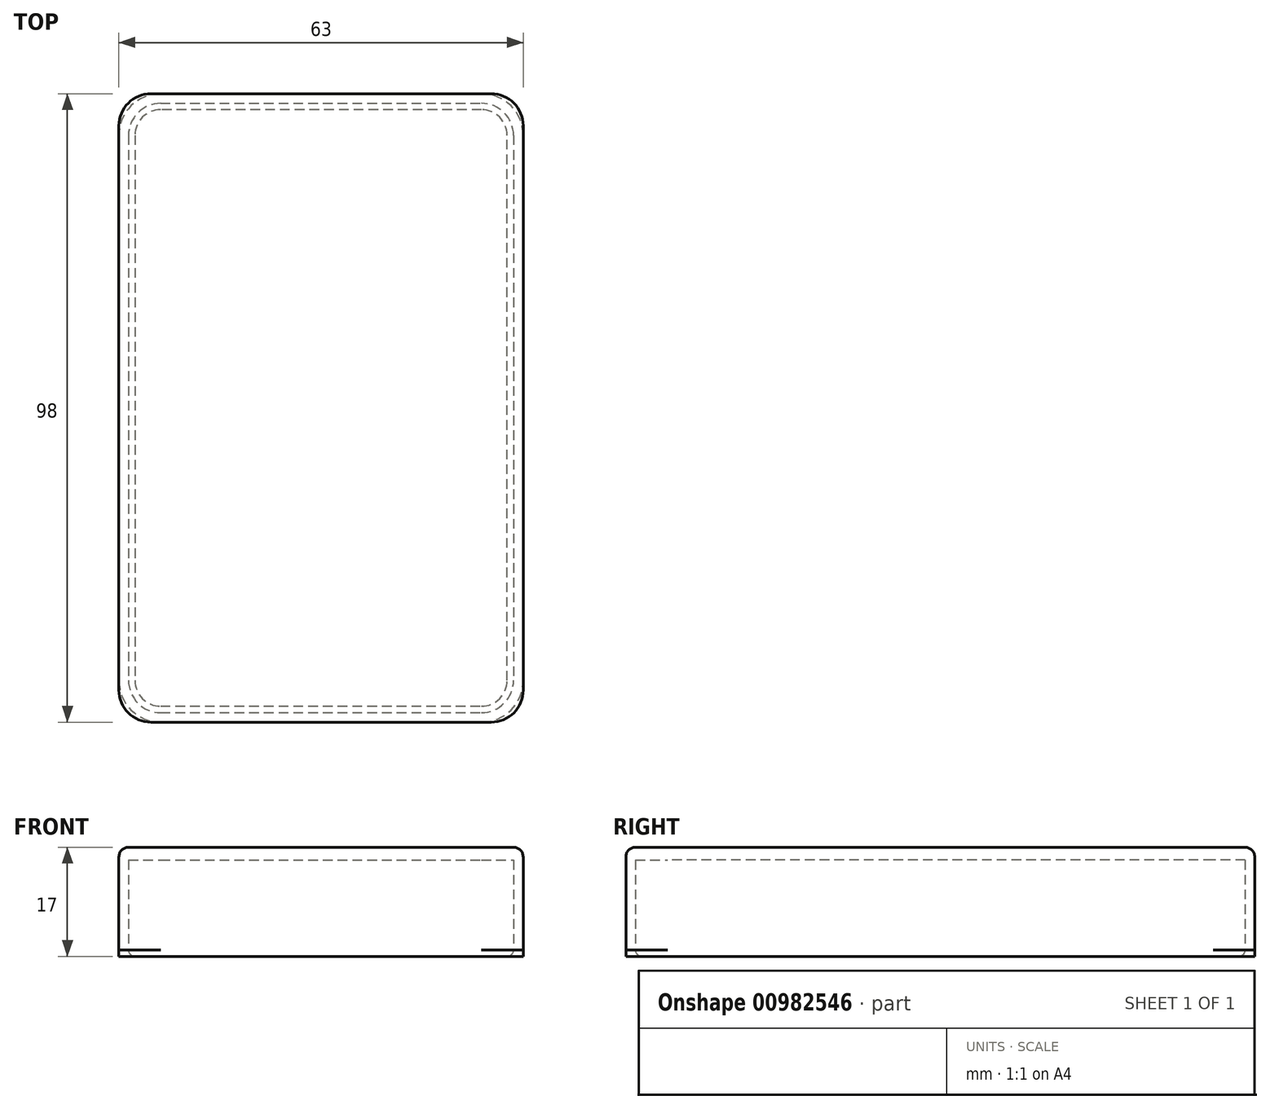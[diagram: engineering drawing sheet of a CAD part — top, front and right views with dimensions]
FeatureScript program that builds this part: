
annotation { "Feature Type Name" : "Feature", "Feature Type Description" : "" }
export const myFeature = defineFeature(function(context is Context, id is Id, definition is map)
    precondition{}
    {
        {
            var Q0;
            Q0=qCreatedBy(makeId("Top.planeOp"),FACE);
            var sketch = newSketch(context, id + "F0", { "sketchPlane" : qUnion([Q0])});
            skLineSegment(sketch, "E0.bottom", {"start": v(-30, 47.5) * mm, "end": v(30, 47.5) * mm});
            skLineSegment(sketch, "E0.top", {"start": v(-30, -47.5) * mm, "end": v(30, -47.5) * mm});
            skLineSegment(sketch, "E0.left", {"start": v(-30, 47.5) * mm, "end": v(-30, -47.5) * mm});
            skLineSegment(sketch, "E0.right", {"start": v(30, 47.5) * mm, "end": v(30, -47.5) * mm});
            skLineSegment(sketch, "E1", {"start": v(-30, 47.5) * mm, "end": v(30, -47.5) * mm, "construction": true});
            skLineSegment(sketch, "E2", {"start": v(30, 47.5) * mm, "end": v(-30, -47.5) * mm, "construction": true});
            skPoint(sketch, "E3", {"position": v(0, 0) * mm});
            skSolve(sketch);
        }
        {
            var Q0;
            Q0=qCreatedBy(makeId("Top.planeOp"),FACE);
            var sketch = newSketch(context, id + "F1", { "sketchPlane" : qUnion([Q0])});
            skLineSegment(sketch, "E4.0", {"start": v(-31.5, 49) * mm, "end": v(-31.5, -49) * mm});
            skLineSegment(sketch, "E4.1", {"start": v(31.5, 49) * mm, "end": v(-31.5, 49) * mm});
            skLineSegment(sketch, "E4.2", {"start": v(31.5, -49) * mm, "end": v(31.5, 49) * mm});
            skLineSegment(sketch, "E4.3", {"start": v(-31.5, -49) * mm, "end": v(31.5, -49) * mm});
            skSolve(sketch);
        }
        {
            var Q0;
            Q0=makeQuery(id+"F1.imprint","IMPRINT",FACE,{"disambiguationData":[TD([[makeQuery(id+"F1.imprint","IMPRINT",EDGE,{"derivedFrom":sQuery(id+"F1.wireOp",EDGE,"E4.0")}),1.0]])]});
            var Q1;
            Q1=sQuery(id+"F1.wireOp",EDGE,"E4.3");
            var Q2;
            Q2=sQuery(id+"F1.wireOp",EDGE,"E4.2");
            var Q3;
            Q3=sQuery(id+"F1.wireOp",EDGE,"E4.0");
            var Q4;
            Q4=sQuery(id+"F0.wireOp",EDGE,"E0.right");
            var Q5;
            Q5=sQuery(id+"F0.wireOp",EDGE,"E0.top");
            var Q6;
            Q6=sQuery(id+"F0.wireOp",EDGE,"E0.bottom");
            var Q7;
            Q7=sQuery(id+"F1.wireOp",EDGE,"E4.1");
            var Q8;
            Q8=sQuery(id+"F0.wireOp",EDGE,"E0.left");
            extrude(context, id + "F2", {"entities" : qUnion([Q0]), "surfaceEntities" : qUnion([Q1, Q2, Q3, Q4, Q5, Q6, Q7, Q8]), "depth" : 16 * mm, "offsetDistance" : 25 * mm});
        }
        {
            var Q0;
            Q0 = qSketchRegion(id + "F0", true);
            var Q1;
            Q1=makeQuery(id+"F2.opExtrude","CAP_FACE",FACE,{"disambiguationData":[OSD([sQuery(id+"F1.wireOp",EDGE,"E4.0"),sQuery(id+"F1.wireOp",EDGE,"E4.1"),sQuery(id+"F1.wireOp",EDGE,"E4.2"),sQuery(id+"F1.wireOp",EDGE,"E4.3")])],"isStart":false});
            extrude(context, id + "F3", {"entities" : qUnion([Q0]), "operationType" : NewBodyOperationType.REMOVE, "endBound" : BoundingType.UP_TO_SURFACE, "depth" : 25 * mm, "endBoundEntityFace" : qUnion([Q1]), "hasOffset" : true, "offsetDistance" : 2 * mm});
        }
        {
            var Q0;
            Q0=makeQuery(id+"F3.boolean.opBoolean","COPY",EDGE,{"derivedFrom":makeQuery(id+"F3.opExtrude","SWEPT_EDGE",EDGE,{"disambiguationData":[OSD([sQuery(id+"F0.wireOp",EDGE,"E0.bottom"),sQuery(id+"F0.wireOp",EDGE,"E0.left")])]})});
            var Q1;
            Q1=makeQuery(id+"F3.boolean.opBoolean","COPY",EDGE,{"derivedFrom":makeQuery(id+"F3.opExtrude","SWEPT_EDGE",EDGE,{"disambiguationData":[OSD([sQuery(id+"F0.wireOp",EDGE,"E0.bottom"),sQuery(id+"F0.wireOp",EDGE,"E0.right")])]})});
            var Q2;
            Q2=makeQuery(id+"F2.opExtrude","SWEPT_EDGE",EDGE,{"disambiguationData":[OSD([sQuery(id+"F1.wireOp",EDGE,"E4.1"),sQuery(id+"F1.wireOp",EDGE,"E4.2")])]});
            var Q3;
            Q3=makeQuery(id+"F2.opExtrude","SWEPT_EDGE",EDGE,{"disambiguationData":[OSD([sQuery(id+"F1.wireOp",EDGE,"E4.0"),sQuery(id+"F1.wireOp",EDGE,"E4.1")])]});
            var Q4;
            Q4=makeQuery(id+"F2.opExtrude","SWEPT_EDGE",EDGE,{"disambiguationData":[OSD([sQuery(id+"F1.wireOp",EDGE,"E4.0"),sQuery(id+"F1.wireOp",EDGE,"E4.3")])]});
            var Q5;
            Q5=makeQuery(id+"F3.boolean.opBoolean","COPY",EDGE,{"derivedFrom":makeQuery(id+"F3.opExtrude","SWEPT_EDGE",EDGE,{"disambiguationData":[OSD([sQuery(id+"F0.wireOp",EDGE,"E0.top"),sQuery(id+"F0.wireOp",EDGE,"E0.left")])]})});
            var Q6;
            Q6=makeQuery(id+"F3.boolean.opBoolean","COPY",EDGE,{"derivedFrom":makeQuery(id+"F3.opExtrude","SWEPT_EDGE",EDGE,{"disambiguationData":[OSD([sQuery(id+"F0.wireOp",EDGE,"E0.top"),sQuery(id+"F0.wireOp",EDGE,"E0.right")])]})});
            var Q7;
            Q7=makeQuery(id+"F2.opExtrude","SWEPT_EDGE",EDGE,{"disambiguationData":[OSD([sQuery(id+"F1.wireOp",EDGE,"E4.2"),sQuery(id+"F1.wireOp",EDGE,"E4.3")])]});
            fillet(context, id + "F4", {"entities" : qUnion([Q0, Q1, Q2, Q3, Q4, Q5, Q6, Q7]), "tangentPropagation" : true, "radius" : 5 * mm, "defaultsChanged" : false, "vertexSettings" : [], "allowEdgeOverflow" : false});
        }
        {
            var Q0;
            Q0=makeQuery(id+"F2.opExtrude","CAP_FACE",FACE,{"disambiguationData":[OSD([sQuery(id+"F1.wireOp",EDGE,"E4.0"),sQuery(id+"F1.wireOp",EDGE,"E4.1"),sQuery(id+"F1.wireOp",EDGE,"E4.2"),sQuery(id+"F1.wireOp",EDGE,"E4.3")])],"isStart":false});
            fillet(context, id + "F5", {"entities" : qUnion([Q0]), "tangentPropagation" : true, "radius" : 1.5 * mm, "defaultsChanged" : false, "vertexSettings" : [], "allowEdgeOverflow" : false});
        }
        {
            var Q0;
            Q0=qCreatedBy(makeId("Top.planeOp"),FACE);
            var sketch = newSketch(context, id + "F6", { "sketchPlane" : qUnion([Q0])});
            skLineSegment(sketch, "E5.0.0", {"start": v(25, -47.5) * mm, "end": v(-25, -47.5) * mm});
            skArc(sketch, "E5.0.1", {"start": v(-25, -47.5) * mm, "mid": v(-28.54, -46.04) * mm, "end": v(-30, -42.5) * mm});
            skLineSegment(sketch, "E5.0.2", {"start": v(-30, -42.5) * mm, "end": v(-30, 42.5) * mm});
            skArc(sketch, "E5.0.3", {"start": v(-30, 42.5) * mm, "mid": v(-28.54, 46.04) * mm, "end": v(-25, 47.5) * mm});
            skLineSegment(sketch, "E5.0.4", {"start": v(-25, 47.5) * mm, "end": v(25, 47.5) * mm});
            skArc(sketch, "E5.0.5", {"start": v(25, 47.5) * mm, "mid": v(28.54, 46.04) * mm, "end": v(30, 42.5) * mm});
            skLineSegment(sketch, "E5.0.6", {"start": v(30, 42.5) * mm, "end": v(30, -42.5) * mm});
            skArc(sketch, "E5.0.7", {"start": v(30, -42.5) * mm, "mid": v(28.54, -46.04) * mm, "end": v(25, -47.5) * mm});
            skSolve(sketch);
        }
        {
            var Q0;
            Q0=qCreatedBy(makeId("Front.planeOp"),FACE);
            var sketch = newSketch(context, id + "F7", { "sketchPlane" : qUnion([Q0])});
            skPoint(sketch, "E6.0", {"position": v(-30, 0) * mm});
            skPoint(sketch, "E7.0", {"position": v(-31.5, 0) * mm});
            skLineSegment(sketch, "E8", {"start": v(-30, 0) * mm, "end": v(-31.5, 0) * mm});
            skLineSegment(sketch, "E9", {"start": v(-31.5, 0) * mm, "end": v(-31.5, -1) * mm});
            skLineSegment(sketch, "E10", {"start": v(-31.5, -1) * mm, "end": v(-30, -1) * mm});
            skArc(sketch, "E11", {"start": v(-30, 0) * mm, "mid": v(-29.7, -0.7) * mm, "end": v(-29, -1) * mm});
            skLineSegment(sketch, "E12", {"start": v(-30, 0) * mm, "end": v(-30, -1) * mm, "construction": true});
            skLineSegment(sketch, "E13", {"start": v(-30, -1) * mm, "end": v(-29, -1) * mm});
            skSolve(sketch);
        }
        {
            var Q0;
            Q0=makeQuery(id+"F7.imprint","IMPRINT",FACE,{"disambiguationData":[TD([[makeQuery(id+"F7.imprint","IMPRINT",EDGE,{"derivedFrom":sQuery(id+"F7.wireOp",EDGE,"E8")}),1.0]])]});
            var Q1;
            Q1=sQuery(id+"F6.wireOp",EDGE,"E5.0.0");
            var Q2;
            Q2=sQuery(id+"F6.wireOp",EDGE,"E5.0.1");
            var Q3;
            Q3=sQuery(id+"F6.wireOp",EDGE,"E5.0.2");
            var Q4;
            Q4=sQuery(id+"F6.wireOp",EDGE,"E5.0.3");
            var Q5;
            Q5=sQuery(id+"F6.wireOp",EDGE,"E5.0.4");
            var Q6;
            Q6=sQuery(id+"F6.wireOp",EDGE,"E5.0.5");
            var Q7;
            Q7=sQuery(id+"F6.wireOp",EDGE,"E5.0.6");
            var Q8;
            Q8=sQuery(id+"F6.wireOp",EDGE,"E5.0.7");
            sweep(context, id + "F8", {"operationType" : NewBodyOperationType.ADD, "profiles" : qUnion([Q0]), "path" : qUnion([Q1, Q2, Q3, Q4, Q5, Q6, Q7, Q8])});
        }
    });
